# Revit family: Geberit Delta ugradni vodokotlić 12 cm, 6 _ 3 litara, sa čeonim aktiviranjem_PRO_100387
name_source: partatom
category: Plumbing Fixtures
units: mm (PartAtom-declared; Revit-internal decimal feet)

## family parameters
Always vertical = Yes
Cut with Voids When Loaded = No
OmniClass Number = 23.31.19.00
Part Type = Normal
Room Calculation Point = Yes
Round Connector Dimension = Use Diameter
Shared = No
Work Plane-Based = No

## types (1)
- 109.100.00.1 Geberit Delta ugradni vodokotlić 12 cm, 6 / 3 litara, sa čeonim aktiviranjem
    B = 410 mm  [stored 1.34514 ft]
    BIM datoteka, datum izmene = 2023.07.05
    BIM datoteka, proizvođač = Geberit
    BIM datoteka, verzija = GEB MG 1.6
    Broj artikla = 109.100.00.1
    CW Connection = Yes
    D1 = 60 mm  [stored 0.19685 ft]
    Default Elevation = 0 mm  [stored 0 ft]
    Description = Geberit Delta ugradni vodokotlić 12 cm, 6 / 3 litara, sa čeonim aktiviranjem
    EAN code basic data = 4025416799658
    Fabrički podešena količina ispiranja = 6 i 3 l
    GEB_culture = sr-RS
    GEB_generic_description = concealed cistern for toilet
    GEB_generic_manufacturer = generic
    GEB_imperial_engineering = No
    GEB_metric_engineering = Yes
    GEB_pimversion = 23.08.11
    GEB_processing_type = T
    GEB_reference = PRO_100387
    GEB_translations = {"ATT_10673":"EAN code basic data","ATT_10773":"Protočni pritisak","ATT_10807":"Opseg podešavanje veće količine vode za ispiranje","ATT_10811":"Opseg podešavanja manje količine vode za ispiranje","ATT_10832":"Maksimalna temperatura vode","ATT_10866":"Fabrički podešena količina ispiranja","GEB_connection_diameter2":"Prečnik priključka 2","applicationPurposes":"Namene","application_range":"Oblast primene","brandName":"Robna marka","characteristics":"Svojstva","connection_description1":"Opis priključka 1","GEB_connection_diameter1":"Prečnik priključka 1","connection_description2":"Opis priključka 2","connection_type_c01":"Vrsta priključka kod priključka 01","connection_type_c02":"Vrsta priključka kod priključka 02","content_creator":"BIM datoteka, proizvođač","content_date_changed":"BIM datoteka, datum izmene","content_version":"BIM datoteka, verzija","key 1000":"Broj artikla","name":"Naziv","productBrand":"Robna marka proizvoda","scopeOfDelivery":"Obim isporuke","type":"Tip","GEB_cut_length_c01":"Maksimalno skraćenje kod priključka 01","angle":"ugao","placement finished floor":"Na gornjoj ivici gotovog poda","sanitary socket":"Spojnica za prelaz","surface height":"Visina debljine poda","warning":"Upozorenje","fixed_material":"Osnovni materijal","fixed_material_01":"Osnovni materijal 01","fixed_material_02":"Osnovni materijal 02","fixed_material_03":"Osnovni materijal 03","ATT_10931":"B","ATT_10951":"H","ATT_380239":"T"}
    GEB_use_DN = Yes
    H = 445 mm  [stored 1.45997 ft]
    HW Connection = No
    IfcDescription = Geberit Delta ugradni vodokotlić 12 cm, 6 / 3 litara, sa čeonim aktiviranjem
    IfcExportAs = IfcSanitaryTerminal
    IfcExportType = CISTERN
    LOD300 = No
    LOD400 = Yes
    Maksimalna temperatura vode = 25 °C
    Manufacturer = Geberit
    Model = Delta 12 cm
    Namene = Za ozidane zidove
Za ugradnju u predzidne konstrukcije delimične ili visine etaže
Za ugradnju u instalacione zidove u visini etaže
Za podne i konzolne WC šolje
Za jednokoličinsko, dvokoličinsko ili start/stop ispiranje
    Naziv = Geberit Delta ugradni vodokotlić 12 cm, 6 / 3 litara, sa čeonim aktiviranjem
    Obim isporuke = Ugaoni ventil R 1/2", kompatibilan sa MF adapterom, sa priključnim prstenom
Građevinska zaštita za revizioni otvor
2 vijka za okvir tipke
Ispirno koleno sa izolacionom oblogama
Zaštitni čep
2 čelične trake za pričvršćenje
2 ugaonika za pričvršćivanje
Materijal za pričvršćivanje
    Oblast primene = sanitary systems
    Opis priključka 1 = cold water in
    Opis priključka 2 = sanitary out
    Opseg podešavanja manje količine vode za ispiranje = 3-4 l
    Opseg podešavanje veće količine vode za ispiranje = 4.5 / 6 / 7.5 l
    Osnovni materijal = Geberit, Plastic, Opaque white
    Osnovni materijal 01 = Geberit, Laminate, Ivory, Matte
    Osnovni materijal 02 = Geberit, Steel, Paint Finish, Black
    Osnovni materijal 03 = Geberit, PE-HD, Black
    Protočni pritisak = 0.1-10 bar
    Robna marka = Geberit
    Svojstva = Ugradni vodokotlić sa aktiviranjem sa prednje strane
Ugradni vodokotlić sa izolacijom protiv kondenzacije
Kod fabričkog podešavanja moguće je automatsko naknadno ispiranje
Ispirno koleno, sakriveno
Priključak za vodu, pozadi ili gore na sredini
Crevo za povezivanje sa ugaonim ventilom koje može da se priključi bez alata
    T = 120 mm  [stored 0.393701 ft]
    Tip = Delta 12 cm
    Vent Connection = No
    Waste Connection = Yes
    cistern_bottom = 445 mm  [stored 1.45997 ft]
    cistern_depth = 120 mm  [stored 0.393701 ft]
    cistern_top_offset = 0 mm  [stored 0 ft]
    cistern_width = 410 mm  [stored 1.34514 ft]
    connection_bend = No
    flushing_water_pipe_D = 105 mm  [stored 0.344488 ft]
    outlet_flow = 0.0 L/s

note: [stored X ft] marks values corroborated as IEEE doubles in the binary element streams (Revit-internal decimal feet)

## geometry (parser evidence)
native form markers: Blend x4, Sweep x8
no freeform markers — native parametric forms only
